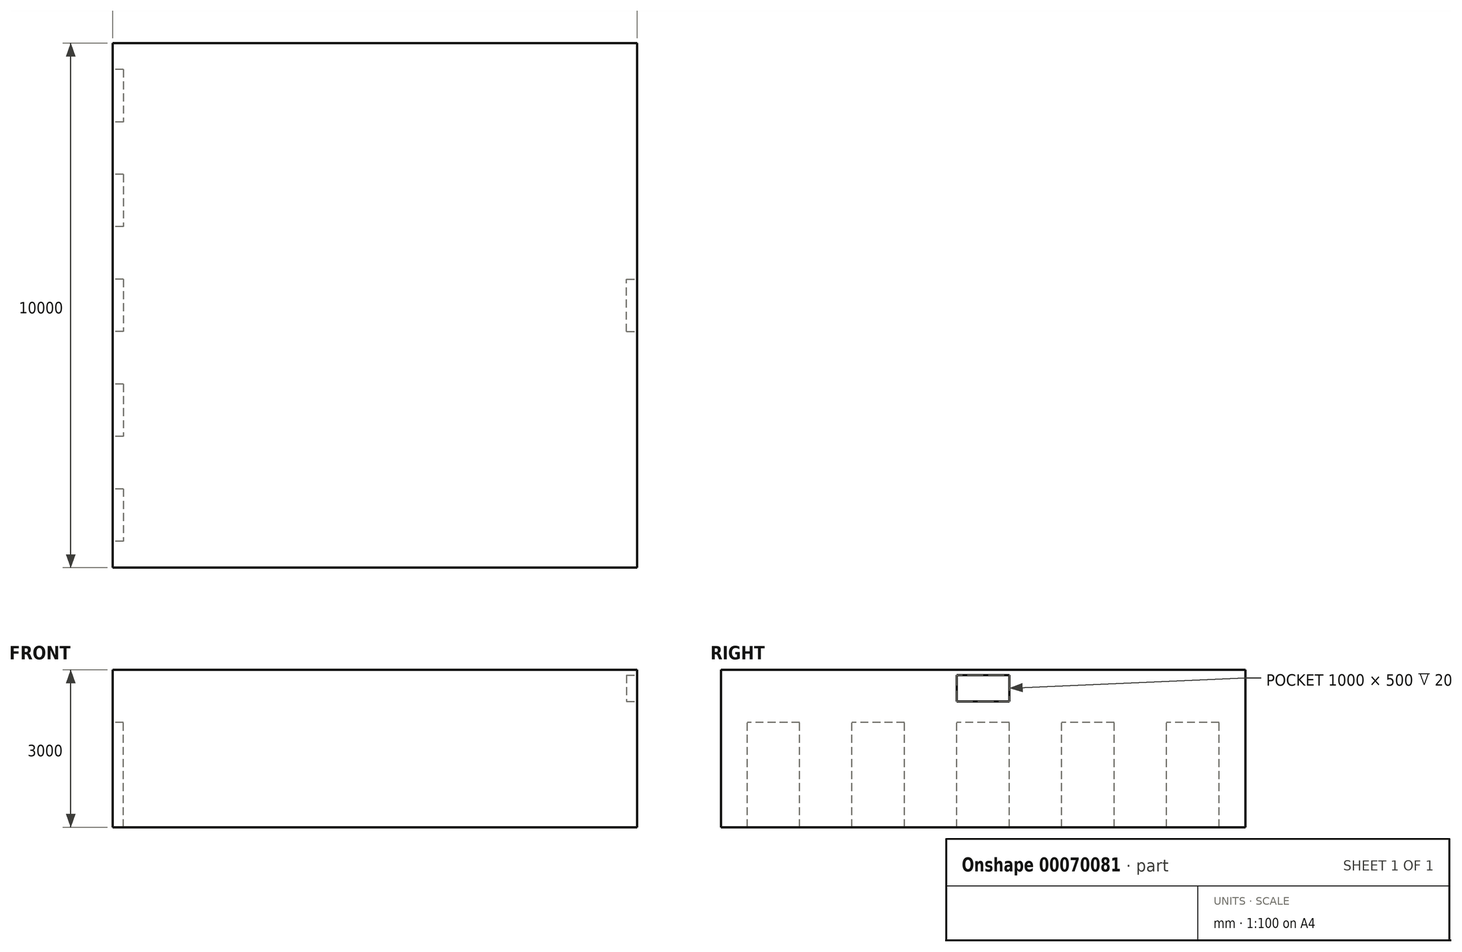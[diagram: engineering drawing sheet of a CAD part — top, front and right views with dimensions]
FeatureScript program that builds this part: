
annotation { "Feature Type Name" : "Feature", "Feature Type Description" : "" }
export const myFeature = defineFeature(function(context is Context, id is Id, definition is map)
    precondition{}
    {
        {
            var Q0;
            Q0=qCreatedBy(makeId("Top.planeOp"),FACE);
            var sketch = newSketch(context, id + "F0", { "sketchPlane" : qUnion([Q0])});
            skLineSegment(sketch, "E0.bottom", {"start": v(0, 10000) * mm, "end": v(10000, 10000) * mm});
            skLineSegment(sketch, "E0.top", {"start": v(0, 0) * mm, "end": v(10000, 0) * mm});
            skLineSegment(sketch, "E0.left", {"start": v(0, 10000) * mm, "end": v(0, 0) * mm});
            skLineSegment(sketch, "E0.right", {"start": v(10000, 10000) * mm, "end": v(10000, 0) * mm});
            skSolve(sketch);
        }
        {
            var Q0;
            Q0=makeQuery(id+"F0.imprint","IMPRINT",FACE,{"disambiguationData":[TD([[makeQuery(id+"F0.imprint","IMPRINT",EDGE,{"derivedFrom":sQuery(id+"F0.wireOp",EDGE,"E0.bottom")}),-1.0]])]});
            extrude(context, id + "F1", {"entities" : qUnion([Q0]), "depth" : 3000 * mm});
        }
        {
            var Q0;
            Q0=makeQuery(id+"F1.opExtrude","SWEPT_FACE",FACE,{"disambiguationData":[OSD([sQuery(id+"F0.wireOp",EDGE,"E0.left")])]});
            var sketch = newSketch(context, id + "F2", { "sketchPlane" : qUnion([Q0])});
            skLineSegment(sketch, "E1.bottom", {"start": v(-9500, 0) * mm, "end": v(-8500, 0) * mm});
            skLineSegment(sketch, "E1.top", {"start": v(-9500, 2000) * mm, "end": v(-8500, 2000) * mm});
            skLineSegment(sketch, "E1.left", {"start": v(-9500, 0) * mm, "end": v(-9500, 2000) * mm});
            skLineSegment(sketch, "E1.right", {"start": v(-8500, 0) * mm, "end": v(-8500, 2000) * mm});
            skLineSegment(sketch, "E2.bottom", {"start": v(-7500, 0) * mm, "end": v(-6500, 0) * mm});
            skLineSegment(sketch, "E2.top", {"start": v(-7500, 2000) * mm, "end": v(-6500, 2000) * mm});
            skLineSegment(sketch, "E2.left", {"start": v(-7500, 0) * mm, "end": v(-7500, 2000) * mm});
            skLineSegment(sketch, "E2.right", {"start": v(-6500, 0) * mm, "end": v(-6500, 2000) * mm});
            skLineSegment(sketch, "E3.bottom", {"start": v(-5500, 0) * mm, "end": v(-4500, 0) * mm});
            skLineSegment(sketch, "E3.top", {"start": v(-5500, 2000) * mm, "end": v(-4500, 2000) * mm});
            skLineSegment(sketch, "E3.left", {"start": v(-5500, 0) * mm, "end": v(-5500, 2000) * mm});
            skLineSegment(sketch, "E3.right", {"start": v(-4500, 0) * mm, "end": v(-4500, 2000) * mm});
            skLineSegment(sketch, "E4.bottom", {"start": v(-3500, 0) * mm, "end": v(-2500, 0) * mm});
            skLineSegment(sketch, "E4.top", {"start": v(-3500, 2000) * mm, "end": v(-2500, 2000) * mm});
            skLineSegment(sketch, "E4.left", {"start": v(-3500, 0) * mm, "end": v(-3500, 2000) * mm});
            skLineSegment(sketch, "E4.right", {"start": v(-2500, 0) * mm, "end": v(-2500, 2000) * mm});
            skLineSegment(sketch, "E5.bottom", {"start": v(-1500, 0) * mm, "end": v(-500, 0) * mm});
            skLineSegment(sketch, "E5.top", {"start": v(-1500, 2000) * mm, "end": v(-500, 2000) * mm});
            skLineSegment(sketch, "E5.left", {"start": v(-1500, 0) * mm, "end": v(-1500, 2000) * mm});
            skLineSegment(sketch, "E5.right", {"start": v(-500, 0) * mm, "end": v(-500, 2000) * mm});
            skSolve(sketch);
        }
        {
            var Q0;
            Q0=makeQuery(id+"F2.imprint","IMPRINT",FACE,{"disambiguationData":[TD([[makeQuery(id+"F2.imprint","IMPRINT",EDGE,{"derivedFrom":sQuery(id+"F2.wireOp",EDGE,"E1.bottom")}),1.0]])]});
            var Q1;
            Q1=makeQuery(id+"F2.imprint","IMPRINT",FACE,{"disambiguationData":[TD([[makeQuery(id+"F2.imprint","IMPRINT",EDGE,{"derivedFrom":sQuery(id+"F2.wireOp",EDGE,"E2.bottom")}),1.0]])]});
            var Q2;
            Q2=makeQuery(id+"F2.imprint","IMPRINT",FACE,{"disambiguationData":[TD([[makeQuery(id+"F2.imprint","IMPRINT",EDGE,{"derivedFrom":sQuery(id+"F2.wireOp",EDGE,"E3.bottom")}),1.0]])]});
            var Q3;
            Q3=makeQuery(id+"F2.imprint","IMPRINT",FACE,{"disambiguationData":[TD([[makeQuery(id+"F2.imprint","IMPRINT",EDGE,{"derivedFrom":sQuery(id+"F2.wireOp",EDGE,"E4.bottom")}),1.0]])]});
            var Q4;
            Q4=makeQuery(id+"F2.imprint","IMPRINT",FACE,{"disambiguationData":[TD([[makeQuery(id+"F2.imprint","IMPRINT",EDGE,{"derivedFrom":sQuery(id+"F2.wireOp",EDGE,"E5.bottom")}),1.0]])]});
            extrude(context, id + "F3", {"entities" : qUnion([Q0, Q1, Q2, Q3, Q4]), "operationType" : NewBodyOperationType.REMOVE, "oppositeDirection" : true, "depth" : 200 * mm});
        }
        {
            var Q0;
            Q0=makeQuery(id+"F1.opExtrude","SWEPT_FACE",FACE,{"disambiguationData":[OSD([sQuery(id+"F0.wireOp",EDGE,"E0.right")])]});
            var sketch = newSketch(context, id + "F4", { "sketchPlane" : qUnion([Q0])});
            skLineSegment(sketch, "E6.bottom", {"start": v(4500, 2900) * mm, "end": v(5500, 2900) * mm});
            skLineSegment(sketch, "E6.top", {"start": v(4500, 2400) * mm, "end": v(5500, 2400) * mm});
            skLineSegment(sketch, "E6.left", {"start": v(4500, 2900) * mm, "end": v(4500, 2400) * mm});
            skLineSegment(sketch, "E6.right", {"start": v(5500, 2900) * mm, "end": v(5500, 2400) * mm});
            skSolve(sketch);
        }
        {
            var Q0;
            Q0=makeQuery(id+"F4.imprint","IMPRINT",FACE,{"disambiguationData":[TD([[makeQuery(id+"F4.imprint","IMPRINT",EDGE,{"derivedFrom":sQuery(id+"F4.wireOp",EDGE,"E6.bottom")}),-1.0]])]});
            extrude(context, id + "F5", {"entities" : qUnion([Q0]), "operationType" : NewBodyOperationType.REMOVE, "oppositeDirection" : true, "depth" : 200 * mm});
        }
    });
